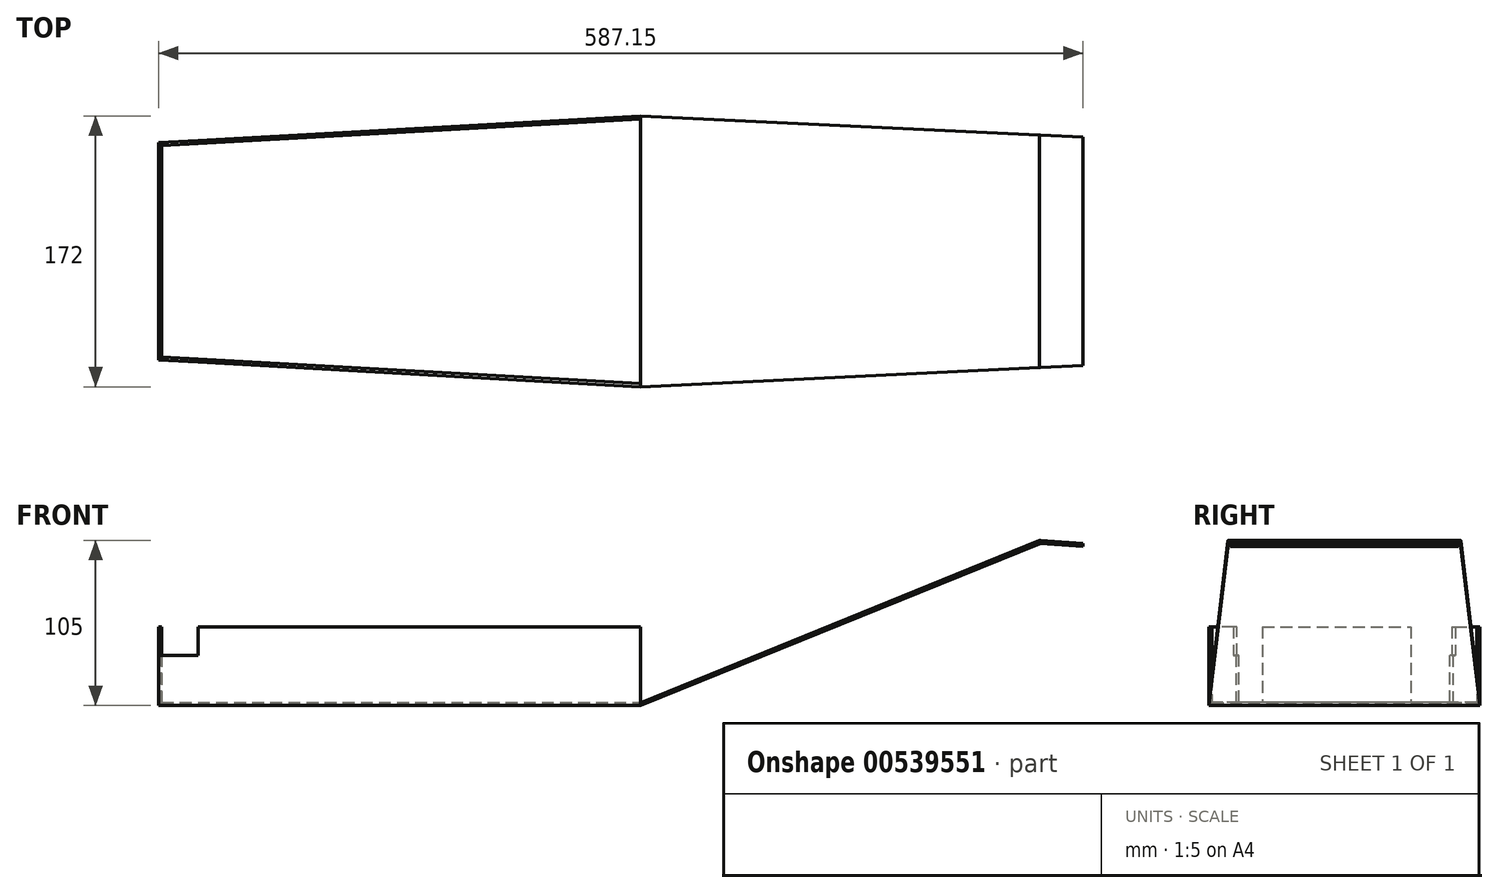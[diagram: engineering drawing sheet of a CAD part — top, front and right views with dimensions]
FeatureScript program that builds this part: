
annotation { "Feature Type Name" : "Feature", "Feature Type Description" : "" }
export const myFeature = defineFeature(function(context is Context, id is Id, definition is map)
    precondition{}
    {
        {
            var Q0;
            Q0=qCreatedBy(makeId("Top.planeOp"),FACE);
            var sketch = newSketch(context, id + "F0", { "sketchPlane" : qUnion([Q0])});
            skLineSegment(sketch, "E0", {"start": v(-306, 0) * mm, "end": v(-306, -69) * mm});
            skLineSegment(sketch, "E1", {"start": v(-306, -69) * mm, "end": v(0, -86) * mm});
            skLineSegment(sketch, "E2", {"start": v(0, -86) * mm, "end": v(302, -71.5) * mm});
            skLineSegment(sketch, "E3", {"start": v(302, -71.5) * mm, "end": v(302, 0) * mm});
            skLineSegment(sketch, "E4", {"start": v(-306, -67) * mm, "end": v(0, -84) * mm});
            skLineSegment(sketch, "E5", {"start": v(0, -84) * mm, "end": v(0, -86) * mm});
            skLineSegment(sketch, "E6.MirrorCS", {"start": v(0, 84) * mm, "end": v(0, 86) * mm});
            skLineSegment(sketch, "E7.MirrorCS", {"start": v(302, 71.5) * mm, "end": v(302, 0) * mm});
            skLineSegment(sketch, "E8.MirrorCS", {"start": v(-306, 67) * mm, "end": v(0, 84) * mm});
            skLineSegment(sketch, "E9.MirrorCS", {"start": v(-306, 69) * mm, "end": v(0, 86) * mm});
            skLineSegment(sketch, "E10.MirrorCS", {"start": v(-306, 0) * mm, "end": v(-306, 69) * mm});
            skLineSegment(sketch, "E11.MirrorCS", {"start": v(0, 86) * mm, "end": v(302, 71.5) * mm});
            skLineSegment(sketch, "E12", {"start": v(-304, 69.11) * mm, "end": v(-304, -69.11) * mm});
            skLineSegment(sketch, "E13", {"start": v(0, 86) * mm, "end": v(302, 86) * mm});
            skLineSegment(sketch, "E14", {"start": v(302, 86) * mm, "end": v(302, 71.5) * mm});
            skLineSegment(sketch, "E15", {"start": v(0, -86) * mm, "end": v(302, -86) * mm});
            skLineSegment(sketch, "E16", {"start": v(302, -86) * mm, "end": v(302, -71.5) * mm});
            skLineSegment(sketch, "E17", {"start": v(0, 86) * mm, "end": v(0, -86) * mm});
            skSolve(sketch);
        }
        {
            var Q0;
            Q0=qCreatedBy(makeId("Front.planeOp"),FACE);
            var sketch = newSketch(context, id + "F1", { "sketchPlane" : qUnion([Q0])});
            skLineSegment(sketch, "E18", {"start": v(0, 0) * mm, "end": v(254, 103) * mm});
            skLineSegment(sketch, "E19", {"start": v(0, 0) * mm, "end": v(0, 1.58) * mm});
            skLineSegment(sketch, "E20", {"start": v(0, 1.58) * mm, "end": v(253.33, 104.88) * mm});
            skLineSegment(sketch, "E21", {"start": v(254, 103) * mm, "end": v(253.33, 104.88) * mm});
            skLineSegment(sketch, "E22", {"start": v(0, 0) * mm, "end": v(254, 0) * mm, "construction": true});
            skLineSegment(sketch, "E23", {"start": v(254, 0) * mm, "end": v(254, 103) * mm, "construction": true});
            skLineSegment(sketch, "E24", {"start": v(254, 103) * mm, "end": v(281, 103) * mm, "construction": true});
            skLineSegment(sketch, "E25", {"start": v(281, 103) * mm, "end": v(281, 101) * mm, "construction": true});
            skLineSegment(sketch, "E26", {"start": v(281, 101) * mm, "end": v(254, 103) * mm});
            skLineSegment(sketch, "E27", {"start": v(281, 101) * mm, "end": v(281.15, 103) * mm});
            skLineSegment(sketch, "E28", {"start": v(281.15, 103) * mm, "end": v(254.22, 104.99) * mm});
            skArc(sketch, "E29", {"start": v(254.22, 104.99) * mm, "mid": v(253.77, 104.98) * mm, "end": v(253.33, 104.88) * mm});
            skSolve(sketch);
        }
        {
            var Q0;
            Q0=makeQuery(id+"F1.imprint","IMPRINT",FACE,{"disambiguationData":[TD([[makeQuery(id+"F1.imprint","IMPRINT",EDGE,{"derivedFrom":sQuery(id+"F1.wireOp",EDGE,"E18")}),1.0]])]});
            extrude(context, id + "F2", {"entities" : qUnion([Q0]), "endBound" : BoundingType.SYMMETRIC, "depth" : 172 * mm, "offsetDistance" : 25 * mm});
        }
        {
            var Q0;
            Q0=makeQuery(id+"F1.imprint","IMPRINT",FACE,{"disambiguationData":[TD([[makeQuery(id+"F1.imprint","IMPRINT",EDGE,{"derivedFrom":sQuery(id+"F1.wireOp",EDGE,"E21")}),-1.0]])]});
            extrude(context, id + "F3", {"entities" : qUnion([Q0]), "operationType" : NewBodyOperationType.ADD, "endBound" : BoundingType.SYMMETRIC, "depth" : 172 * mm, "offsetDistance" : 25 * mm});
        }
        {
            var Q0;
            Q0=makeQuery(id+"F0.imprint","IMPRINT",FACE,{"disambiguationData":[TD([[makeQuery(id+"F0.imprint","IMPRINT",EDGE,{"derivedFrom":sQuery(id+"F0.wireOp",EDGE,"E2")}),-1.0]])]});
            var Q1;
            Q1=makeQuery(id+"F0.imprint","IMPRINT",FACE,{"disambiguationData":[TD([[makeQuery(id+"F0.imprint","IMPRINT",EDGE,{"derivedFrom":sQuery(id+"F0.wireOp",EDGE,"E11.MirrorCS")}),1.0]])]});
            extrude(context, id + "F4", {"entities" : qUnion([Q0, Q1]), "operationType" : NewBodyOperationType.REMOVE, "depth" : 121 * mm, "offsetDistance" : 25 * mm});
        }
        {
            var Q0;
            {var subQ0=sQuery(id+"F0.wireOp",EDGE,"E10.MirrorCS");var subQ1=sQuery(id+"F0.wireOp",EDGE,"E0");var subQ2=makeQuery(id+"F0.imprint","INTERSECT",VERTEX,{"derivedFrom":[subQ1,subQ0]});Q0=makeQuery(id+"F0.imprint","IMPRINT",FACE,{"disambiguationData":[TD([[makeQuery(id+"F0.imprint","IMPRINT",EDGE,{"disambiguationData":[TD([[subQ2,-1.0]])],"derivedFrom":subQ1}),1.0]])]});}
            var Q1;
            {var subQ0=sQuery(id+"F0.wireOp",EDGE,"E17");var subQ5=sQuery(id+"F0.wireOp",EDGE,"E4");var subQ7=makeQuery(id+"F0.imprint","INTERSECT",VERTEX,{"derivedFrom":[subQ5,subQ0]});Q1=makeQuery(id+"F0.imprint","IMPRINT",FACE,{"disambiguationData":[TD([[makeQuery(id+"F0.imprint","IMPRINT",EDGE,{"disambiguationData":[TD([[subQ7,1.0]])],"derivedFrom":subQ5}),-1.0]])]});}
            var Q2;
            {var subQ0=sQuery(id+"F0.wireOp",EDGE,"E17");var subQ1=sQuery(id+"F0.wireOp",EDGE,"E8.MirrorCS");var subQ2=makeQuery(id+"F0.imprint","INTERSECT",VERTEX,{"derivedFrom":[subQ1,subQ0]});Q2=makeQuery(id+"F0.imprint","IMPRINT",FACE,{"disambiguationData":[TD([[makeQuery(id+"F0.imprint","IMPRINT",EDGE,{"disambiguationData":[TD([[subQ2,1.0]])],"derivedFrom":subQ1}),1.0]])]});}
            var Q3;
            {var subQ0=sQuery(id+"F0.wireOp",EDGE,"E1");var subQ1=sQuery(id+"F0.wireOp",EDGE,"E0");var subQ2=makeQuery(id+"F0.imprint","INTERSECT",VERTEX,{"derivedFrom":[subQ1,subQ0]});Q3=makeQuery(id+"F0.imprint","IMPRINT",FACE,{"disambiguationData":[TD([[makeQuery(id+"F0.imprint","IMPRINT",EDGE,{"disambiguationData":[TD([[subQ2,1.0]])],"derivedFrom":subQ1}),1.0]])]});}
            var Q4;
            {var subQ0=sQuery(id+"F0.wireOp",EDGE,"E10.MirrorCS");var subQ1=sQuery(id+"F0.wireOp",EDGE,"E8.MirrorCS");var subQ2=makeQuery(id+"F0.imprint","INTERSECT",VERTEX,{"derivedFrom":[subQ1,subQ0]});Q4=makeQuery(id+"F0.imprint","IMPRINT",FACE,{"disambiguationData":[TD([[makeQuery(id+"F0.imprint","IMPRINT",EDGE,{"disambiguationData":[TD([[subQ2,-1.0]])],"derivedFrom":subQ1}),1.0]])]});}
            extrude(context, id + "F5", {"entities" : qUnion([Q0, Q1, Q2, Q3, Q4]), "operationType" : NewBodyOperationType.ADD, "depth" : 50 * mm, "offsetDistance" : 25 * mm});
        }
        {
            var Q0;
            {var subQ0=sQuery(id+"F0.wireOp",EDGE,"E17");var subQ1=sQuery(id+"F0.wireOp",EDGE,"E4");var subQ2=makeQuery(id+"F0.imprint","INTERSECT",VERTEX,{"derivedFrom":[subQ1,subQ0]});Q0=makeQuery(id+"F0.imprint","IMPRINT",FACE,{"disambiguationData":[TD([[makeQuery(id+"F0.imprint","IMPRINT",EDGE,{"disambiguationData":[TD([[subQ2,1.0]])],"derivedFrom":subQ1}),1.0]])]});}
            extrude(context, id + "F6", {"entities" : qUnion([Q0]), "depth" : 2 * mm, "offsetDistance" : 25 * mm});
        }
        {
            var Q0;
            Q0=makeQuery(id+"F5.opExtrude","SWEPT_FACE",FACE,{"disambiguationData":[OSD([sQuery(id+"F0.wireOp",EDGE,"E12")])]});
            var sketch = newSketch(context, id + "F7", { "sketchPlane" : qUnion([Q0])});
            skLineSegment(sketch, "E30", {"start": v(-67.11, 0) * mm, "end": v(-67.11, 2) * mm, "construction": true});
            skLineSegment(sketch, "E31", {"start": v(-67.11, 2) * mm, "end": v(-52.11, 2) * mm});
            skLineSegment(sketch, "E32", {"start": v(-52.11, 2) * mm, "end": v(-52.11, 50) * mm});
            skLineSegment(sketch, "E33", {"start": v(-52.11, 50) * mm, "end": v(-67.11, 50) * mm});
            skLineSegment(sketch, "E34", {"start": v(-67.11, 50) * mm, "end": v(-67.11, 2) * mm});
            skLineSegment(sketch, "E35", {"start": v(67.11, 0) * mm, "end": v(67.11, 2) * mm, "construction": true});
            skLineSegment(sketch, "E36", {"start": v(67.11, 2) * mm, "end": v(42.11, 2) * mm});
            skLineSegment(sketch, "E37", {"start": v(42.11, 2) * mm, "end": v(42.11, 50) * mm});
            skLineSegment(sketch, "E38", {"start": v(42.11, 50) * mm, "end": v(67.11, 50) * mm});
            skLineSegment(sketch, "E39", {"start": v(67.11, 50) * mm, "end": v(67.11, 2) * mm});
            skSolve(sketch);
        }
        {
            var Q0;
            Q0=makeQuery(id+"F7.imprint","IMPRINT",FACE,{"disambiguationData":[TD([[makeQuery(id+"F7.imprint","IMPRINT",EDGE,{"derivedFrom":sQuery(id+"F7.wireOp",EDGE,"E31")}),1.0]])]});
            var Q1;
            Q1=makeQuery(id+"F7.imprint","IMPRINT",FACE,{"disambiguationData":[TD([[makeQuery(id+"F7.imprint","IMPRINT",EDGE,{"derivedFrom":sQuery(id+"F7.wireOp",EDGE,"E36")}),-1.0]])]});
            extrude(context, id + "F8", {"entities" : qUnion([Q0, Q1]), "operationType" : NewBodyOperationType.REMOVE, "oppositeDirection" : true, "depth" : 50 * mm, "offsetDistance" : 25 * mm});
        }
        {
            var Q0;
            Q0=makeQuery(id+"F5.opExtrude","SWEPT_FACE",FACE,{"disambiguationData":[OSD([sQuery(id+"F0.wireOp",EDGE,"E1")])]});
            var sketch = newSketch(context, id + "F9", { "sketchPlane" : qUnion([Q0])});
            skLineSegment(sketch, "E40", {"start": v(-301.7, 50) * mm, "end": v(-276.7, 50) * mm});
            skLineSegment(sketch, "E41", {"start": v(-276.7, 50) * mm, "end": v(-276.7, 32) * mm});
            skLineSegment(sketch, "E42", {"start": v(-276.7, 32) * mm, "end": v(-301.7, 32) * mm});
            skLineSegment(sketch, "E43", {"start": v(-301.7, 32) * mm, "end": v(-301.7, 50) * mm});
            skSolve(sketch);
        }
        {
            var Q0;
            Q0=makeQuery(id+"F9.imprint","IMPRINT",FACE,{"disambiguationData":[TD([[makeQuery(id+"F9.imprint","IMPRINT",EDGE,{"derivedFrom":sQuery(id+"F9.wireOp",EDGE,"E40")}),-1.0]])]});
            extrude(context, id + "F10", {"entities" : qUnion([Q0]), "operationType" : NewBodyOperationType.REMOVE, "oppositeDirection" : true, "depth" : 5 * mm, "offsetDistance" : 25 * mm});
        }
        {
            var Q0;
            Q0=makeQuery(id+"F10.boolean.opBoolean","COPY",FACE,{"derivedFrom":makeQuery(id+"F10.opExtrude","SWEPT_FACE",FACE,{"disambiguationData":[OSD([sQuery(id+"F9.wireOp",EDGE,"E43")])]})});
            extrude(context, id + "F11", {"entities" : qUnion([Q0]), "operationType" : NewBodyOperationType.REMOVE, "oppositeDirection" : true, "depth" : 25 * mm, "offsetDistance" : 25 * mm});
        }
        {
            var Q0;
            Q0=makeQuery(id+"F5.opExtrude","SWEPT_FACE",FACE,{"disambiguationData":[OSD([sQuery(id+"F0.wireOp",EDGE,"E9.MirrorCS")])]});
            var sketch = newSketch(context, id + "F12", { "sketchPlane" : qUnion([Q0])});
            skLineSegment(sketch, "E44", {"start": v(301.7, 50) * mm, "end": v(276.7, 50) * mm});
            skLineSegment(sketch, "E45", {"start": v(276.7, 50) * mm, "end": v(276.7, 32) * mm});
            skLineSegment(sketch, "E46", {"start": v(276.7, 32) * mm, "end": v(301.7, 32) * mm});
            skLineSegment(sketch, "E47", {"start": v(301.7, 32) * mm, "end": v(301.7, 50) * mm});
            skSolve(sketch);
        }
        {
            var Q0;
            Q0=makeQuery(id+"F12.imprint","IMPRINT",FACE,{"disambiguationData":[TD([[makeQuery(id+"F12.imprint","IMPRINT",EDGE,{"derivedFrom":sQuery(id+"F12.wireOp",EDGE,"E44")}),1.0]])]});
            extrude(context, id + "F13", {"entities" : qUnion([Q0]), "operationType" : NewBodyOperationType.REMOVE, "oppositeDirection" : true, "depth" : 5 * mm, "offsetDistance" : 25 * mm});
        }
        {
            var Q0;
            Q0=makeQuery(id+"F13.boolean.opBoolean","COPY",FACE,{"derivedFrom":makeQuery(id+"F13.opExtrude","SWEPT_FACE",FACE,{"disambiguationData":[OSD([sQuery(id+"F12.wireOp",EDGE,"E47")])]})});
            extrude(context, id + "F14", {"entities" : qUnion([Q0]), "operationType" : NewBodyOperationType.REMOVE, "oppositeDirection" : true, "depth" : 25 * mm, "offsetDistance" : 25 * mm});
        }
    });
